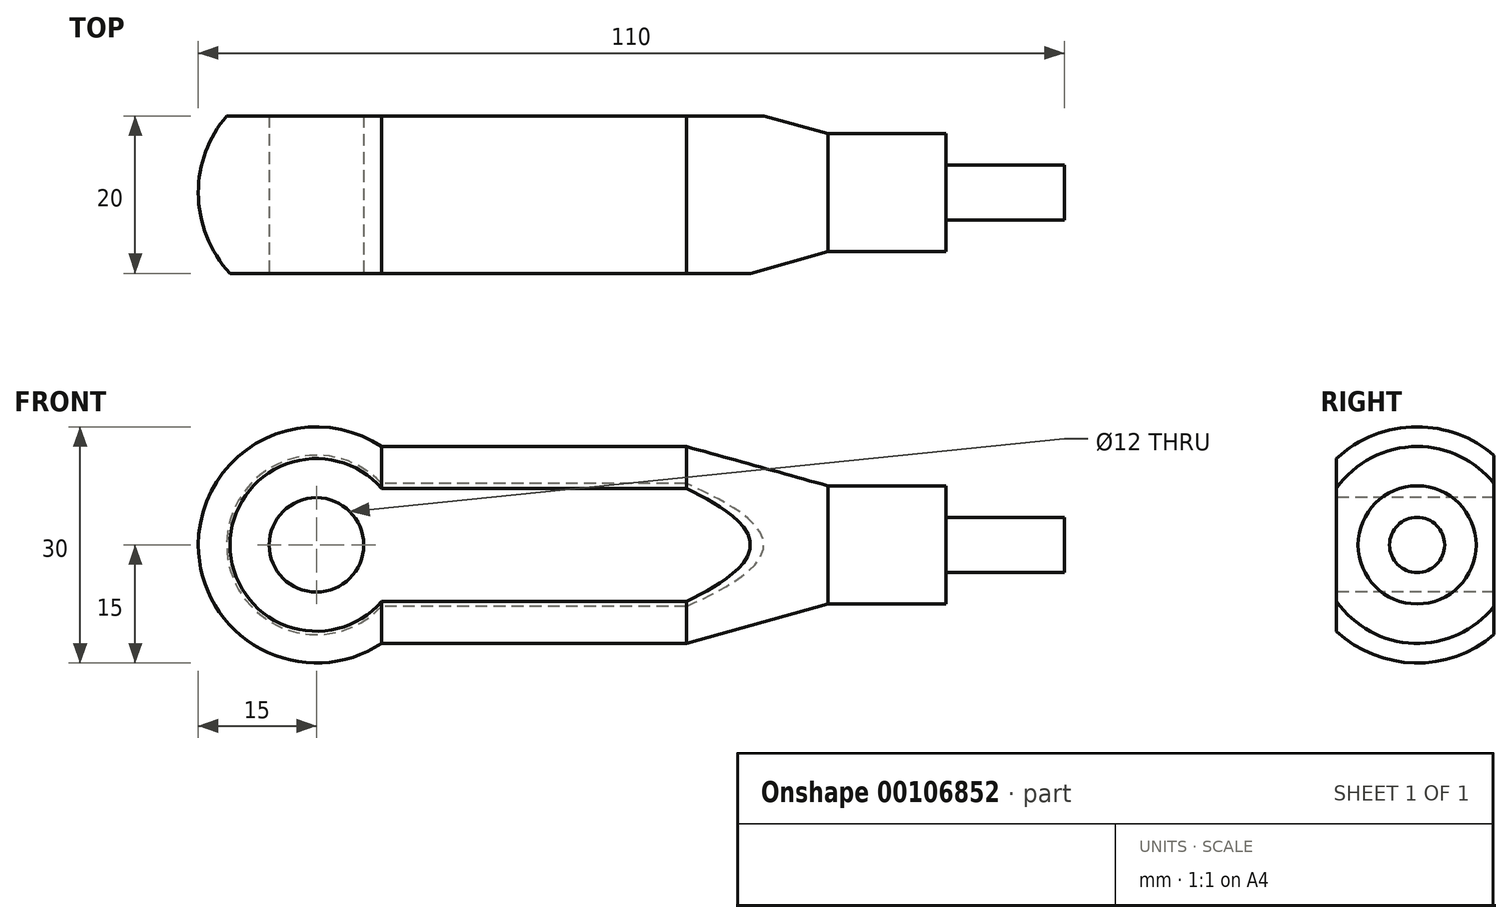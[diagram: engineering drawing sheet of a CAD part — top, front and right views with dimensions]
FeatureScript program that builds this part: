
annotation { "Feature Type Name" : "Feature", "Feature Type Description" : "" }
export const myFeature = defineFeature(function(context is Context, id is Id, definition is map)
    precondition{}
    {
        {
            var Q0;
            Q0=qCreatedBy(makeId("Front.planeOp"),FACE);
            var sketch = newSketch(context, id + "F0", { "sketchPlane" : qUnion([Q0])});
            skLineSegment(sketch, "E0", {"start": v(0, 0) * mm, "end": v(121.74, 0) * mm, "construction": true});
            skLineSegment(sketch, "E1", {"start": v(23.3, 12.5) * mm, "end": v(62, 12.5) * mm});
            skArc(sketch, "E2", {"start": v(23.3, 12.5) * mm, "mid": v(7.9, 13.22) * mm, "end": v(0, 0) * mm});
            skLineSegment(sketch, "E3", {"start": v(62, 12.5) * mm, "end": v(80, 7.5) * mm});
            skLineSegment(sketch, "E4", {"start": v(80, 7.5) * mm, "end": v(95, 7.5) * mm});
            skLineSegment(sketch, "E5", {"start": v(110, 0) * mm, "end": v(0, 0) * mm});
            skLineSegment(sketch, "E6", {"start": v(62, 12.5) * mm, "end": v(62, 0) * mm});
            skLineSegment(sketch, "E7", {"start": v(80, 7.5) * mm, "end": v(80, 0) * mm});
            skLineSegment(sketch, "E8", {"start": v(95, 7.5) * mm, "end": v(95, 0) * mm});
            skLineSegment(sketch, "E9", {"start": v(95, 3.5) * mm, "end": v(110, 3.5) * mm});
            skLineSegment(sketch, "E10", {"start": v(110, 3.5) * mm, "end": v(110, 0) * mm});
            skLineSegment(sketch, "E11", {"start": v(15, 0) * mm, "end": v(15, -43.82) * mm, "construction": true});
            skSolve(sketch);
        }
        {
            var Q0;
            Q0 = qSketchRegion(id + "F0", true);
            var Q1;
            Q1=sQuery(id+"F0.wireOp",EDGE,"E0");
            revolve(context, id + "F1", {"entities" : qUnion([Q0]), "axis" : qUnion([Q1]), "revolveType" : RevolveType.FULL});
        }
        {
            var Q0;
            Q0=qCreatedBy(makeId("Front.planeOp"),FACE);
            var sketch = newSketch(context, id + "F2", { "sketchPlane" : qUnion([Q0])});
            skCircle(sketch, "E12", {"center": v(15, 0) * mm, "radius": 6 * mm});
            skSolve(sketch);
        }
        {
            var Q0;
            Q0 = qSketchRegion(id + "F2", true);
            extrude(context, id + "F3", {"entities" : qUnion([Q0]), "operationType" : NewBodyOperationType.REMOVE, "endBound" : BoundingType.SYMMETRIC, "oppositeDirection" : true, "depth" : 100 * mm});
        }
        {
            var Q0;
            Q0=qCreatedBy(makeId("Top.planeOp"),FACE);
            var sketch = newSketch(context, id + "F4", { "sketchPlane" : qUnion([Q0])});
            skLineSegment(sketch, "E13.bottom", {"start": v(0, 0) * mm, "end": v(74.73, 0) * mm});
            skLineSegment(sketch, "E13.top", {"start": v(0, -10.24) * mm, "end": v(74.73, -10.24) * mm});
            skLineSegment(sketch, "E13.left", {"start": v(0, 0) * mm, "end": v(0, -10.24) * mm});
            skLineSegment(sketch, "E13.right", {"start": v(74.73, 0) * mm, "end": v(74.73, -10.24) * mm});
            skLineSegment(sketch, "E14.top", {"start": v(0, 9.76) * mm, "end": v(74.73, 9.76) * mm});
            skLineSegment(sketch, "E14.left", {"start": v(0, 0) * mm, "end": v(0, 9.76) * mm});
            skLineSegment(sketch, "E14.right", {"start": v(74.73, 0) * mm, "end": v(74.73, 9.76) * mm});
            skLineSegment(sketch, "E15.bottom", {"start": v(74.58, -15) * mm, "end": v(-74.58, -15) * mm});
            skLineSegment(sketch, "E15.top", {"start": v(74.58, 15) * mm, "end": v(-74.58, 15) * mm});
            skLineSegment(sketch, "E15.left", {"start": v(74.58, -15) * mm, "end": v(74.58, 15) * mm});
            skLineSegment(sketch, "E15.right", {"start": v(-74.58, -15) * mm, "end": v(-74.58, 15) * mm});
            skPoint(sketch, "E15.middle", {"position": v(0, 0) * mm});
            skSolve(sketch);
        }
        {
            var Q0;
            {var subQ4=sQuery(id+"F4.wireOp",EDGE,"E13.left");Q0=makeQuery(id+"F4.imprint","IMPRINT",FACE,{"disambiguationData":[TD([[makeQuery(id+"F4.imprint","IMPRINT",EDGE,{"derivedFrom":subQ4}),-1.0]])]});}
            extrude(context, id + "F5", {"entities" : qUnion([Q0]), "operationType" : NewBodyOperationType.REMOVE, "endBound" : BoundingType.SYMMETRIC, "depth" : 50 * mm});
        }
    });
